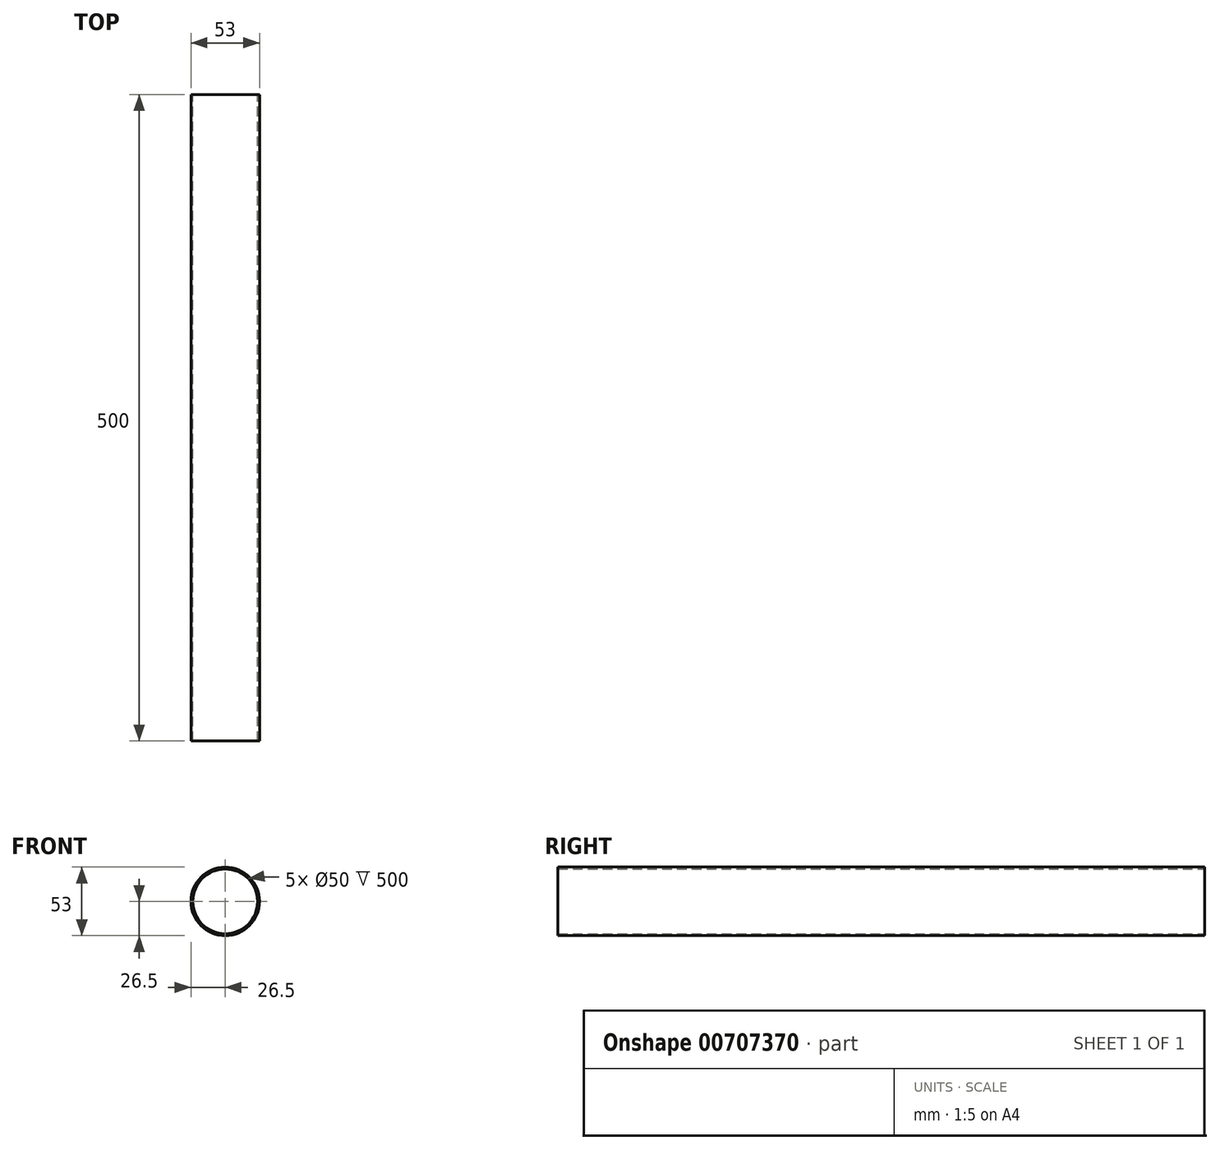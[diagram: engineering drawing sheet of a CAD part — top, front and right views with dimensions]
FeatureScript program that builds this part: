
annotation { "Feature Type Name" : "Feature", "Feature Type Description" : "" }
export const myFeature = defineFeature(function(context is Context, id is Id, definition is map)
    precondition{}
    {
        {
            var Q0;
            Q0=qCreatedBy(makeId("Front.planeOp"),FACE);
            var sketch = newSketch(context, id + "F0", { "sketchPlane" : qUnion([Q0])});
            skCircle(sketch, "E0", {"center": v(0, 0) * mm, "radius": 26.5 * mm});
            skCircle(sketch, "E1", {"center": v(0, 0) * mm, "radius": 25 * mm});
            skSolve(sketch);
        }
        {
            var Q0;
            Q0=makeQuery(id+"F0.imprint","IMPRINT",FACE,{"disambiguationData":[TD([[makeQuery(id+"F0.imprint","IMPRINT",EDGE,{"derivedFrom":sQuery(id+"F0.wireOp",EDGE,"E0")}),1.0]])]});
            extrude(context, id + "F1", {"entities" : qUnion([Q0]), "endBound" : BoundingType.SYMMETRIC, "depth" : 500 * mm, "offsetDistance" : 25 * mm});
        }
    });
